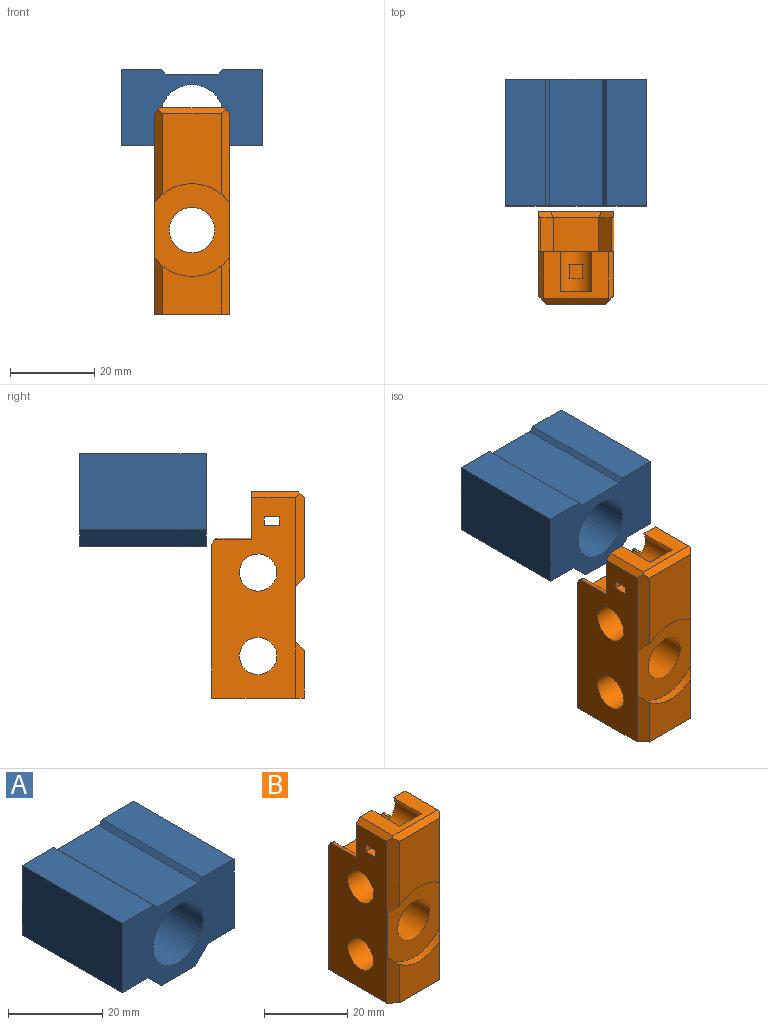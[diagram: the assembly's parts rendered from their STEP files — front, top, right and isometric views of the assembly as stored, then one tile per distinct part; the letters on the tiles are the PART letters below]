
ASSEMBLY  parts=2 mates=1
PART A: 15 faces, bbox 33.5x30x22 mm
  f0: plane 30x18mm, normal (-1,0,0), area 540mm2, adj f1,f12,f13,f14
  f1: plane 30x7.75mm, normal (0,0,-1), area 232.5mm2, adj f0,f2,f13,f14
  f2: plane 30x4mm, normal (-0.71,0,-0.71), area 169.7mm2, adj f1,f3,f13,f14
  f3: plane 30x10mm, normal (0,0,-1), area 300mm2, adj f2,f4,f13,f14
  f4: plane 30x4mm, normal (0.71,0,-0.71), area 169.7mm2, adj f3,f5,f13,f14
  f5: plane 30x7.75mm, normal (0,0,-1), area 232.5mm2, adj f4,f6,f13,f14
  f6: plane 30x18mm, normal (1,0,0), area 540mm2, adj f5,f7,f13,f14
  f7: plane 30x9.5mm, normal (0,0,1), area 285mm2, adj f6,f8,f13,f14
  f8: plane 30x1mm, normal (-0.71,0,0.71), area 42.4mm2, adj f7,f9,f13,f14
  f9: plane 30x12.5mm, normal (0,0,1), area 375mm2, adj f8,f10,f13,f14
  f10: plane 30x1mm, normal (0.71,0,0.71), area 42.4mm2, adj f9,f12,f13,f14
  f11: cylinder r=7.5mm len=30mm, axis (0,1,0), area 1413.7mm2, adj f13,f14
  f12: plane 30x9.5mm, normal (0,0,1), area 285mm2, adj f0,f10,f13,f14
  f13: plane 33.5x22mm, normal (0,-1,0), area 468.8mm2, adj f0,f1,f2,f3,f4,f5,f6,f7
  f14: plane 33.5x22mm, normal (0,1,0), area 468.8mm2, adj f0,f1,f2,f3,f4,f5,f6,f7
PART B: 40 faces, bbox 18x22x49 mm
  f0: plane 7.57x3.5mm, normal (0,0,-1), area 26.5mm2, adj f2,f14,f16,f28
  f1: plane 36.51x18mm, normal (0,1,0), area 521.6mm2, adj f2,f4,f6,f8,f33,f34,f35
  f2: plane 47.6x19.9mm, normal (-1,0,0), area 722.1mm2, adj f0,f1,f8,f9,f10,f11,f12,f14
  f3: plane 19.08x13.8mm, normal (0,-1,0), area 240.4mm2, adj f23,f32,f38,f39
  f4: plane 47.6x19.9mm, normal (1,0,0), area 722.1mm2, adj f1,f8,f9,f10,f11,f12,f13,f14
  f5: plane 13.8x11.38mm, normal (0,-1,0), area 134.2mm2, adj f8,f22,f38,f39
  f6: cylinder r=5.38mm len=20mm, axis (0,-1,0), area 675.4mm2, adj f1,f24
  f7: plane 15.2x11.1mm, normal (0,0,1), area 99.1mm2, adj f21,f28,f29,f30,f31,f32
  f8: plane 22x18mm, normal (0,0,-1), area 391.6mm2, adj f1,f2,f4,f5,f38,f39
  f9: plane 18x0.39mm, normal (0,0.71,0.71), area 9.8mm2, adj f2,f4,f10,f12
  f10: cylinder r=4.4mm len=18mm, axis (1,0,0), area 435.4mm2, adj f2,f4,f9,f11
  f11: plane 18x0.39mm, normal (0,0.71,-0.71), area 9.8mm2, adj f2,f4,f10,f12
  f12: plane 18x2.6mm, normal (0,1,0), area 46.8mm2, adj f2,f4,f9,f11
  f13: plane 7.57x3.5mm, normal (0,0,-1), area 26.5mm2, adj f4,f14,f16,f28
  f14: plane 18x2mm, normal (0,1,0), area 35.5mm2, adj f0,f2,f4,f13,f15,f28
  f15: plane 18x3.5mm, normal (0,0,1), area 63mm2, adj f2,f4,f14,f16
  f16: plane 18x2mm, normal (0,-1,0), area 35.5mm2, adj f0,f2,f4,f13,f15,f28
  f17: cylinder r=4.4mm len=18mm, axis (1,0,0), area 435.4mm2, adj f2,f4,f18,f20
  f18: plane 18x0.39mm, normal (0,0.71,-0.71), area 9.8mm2, adj f2,f4,f17,f19
  f19: plane 18x2.6mm, normal (0,1,0), area 46.8mm2, adj f2,f4,f18,f20
  f20: plane 18x0.39mm, normal (0,0.71,0.71), area 9.8mm2, adj f2,f4,f17,f19
  f21: plane 18x14.05mm, normal (0,1,0), area 194.3mm2, adj f2,f4,f7,f25,f26,f27,f28,f30
  f22: cylinder r=11mm len=17.8mm, axis (0,-1,0), area 35.4mm2, adj f5,f24,f38,f39
  f23: cylinder r=11mm len=17.8mm, axis (0,-1,0), area 35.4mm2, adj f3,f24,f38,f39
  f24: plane 22x17.8mm, normal (0,-1,0), area 252.4mm2, adj f6,f22,f23,f38,f39
  f25: plane 8.07x2.9mm, normal (-0.71,0,0.71), area 33.1mm2, adj f21,f26,f35,f36
  f26: plane 10.83x8.07mm, normal (0,0,1), area 87.4mm2, adj f21,f25,f27,f34
  f27: plane 8.07x2.9mm, normal (0.71,0,0.71), area 33.1mm2, adj f21,f26,f33,f37
  f28: cylinder r=4.2mm len=9.5mm, axis (0,1,0), area 155.8mm2, adj f0,f7,f13,f14,f16,f21,f29
  f29: plane 8.4x6.25mm, normal (0,1,0), area 44.2mm2, adj f7,f28
  f30: plane 11.45x1.4mm, normal (0.71,0,0.71), area 21.8mm2, adj f4,f7,f21,f32,f39
  f31: plane 11.45x1.4mm, normal (-0.71,0,0.71), area 21.8mm2, adj f2,f7,f21,f32,f38
  f32: plane 15.9x1.4mm, normal (0,-0.71,0.71), area 29.7mm2, adj f3,f7,f30,f31,f38,f39
  f33: plane 4.45x3.59mm, normal (0.5,0.71,0.5), area 9.1mm2, adj f1,f2,f27,f34,f37
  f34: plane 12.01x1.43mm, normal (0,0.71,0.71), area 23.1mm2, adj f1,f26,f33,f35
  f35: plane 4.45x3.59mm, normal (-0.5,0.71,0.5), area 9.1mm2, adj f1,f4,f25,f34,f36
  f36: cylinder r=0.4mm len=8.75mm, axis (0,-1,0), area 7.9mm2, adj f4,f21,f25,f35
  f37: cylinder r=0.4mm len=8.75mm, axis (0,1,0), area 7.9mm2, adj f2,f21,f27,f33
  f38: plane 48.65x2.1mm, normal (-0.71,-0.71,0), area 99.9mm2, adj f2,f3,f5,f8,f22,f23,f24,f31
  f39: plane 48.65x2.1mm, normal (0.71,-0.71,0), area 99.9mm2, adj f3,f4,f5,f8,f22,f23,f24,f30
PLACE A rot(axis=(0,1,0),0deg) t=(-3.78,47.01,37.98)mm
PLACE B t=(-3.78,4.69,-8.97)mm fixed
MATE slider A.f11 <-> B.f28  axis (0,1,0) through (-3.78,17.01,37.98)mm
